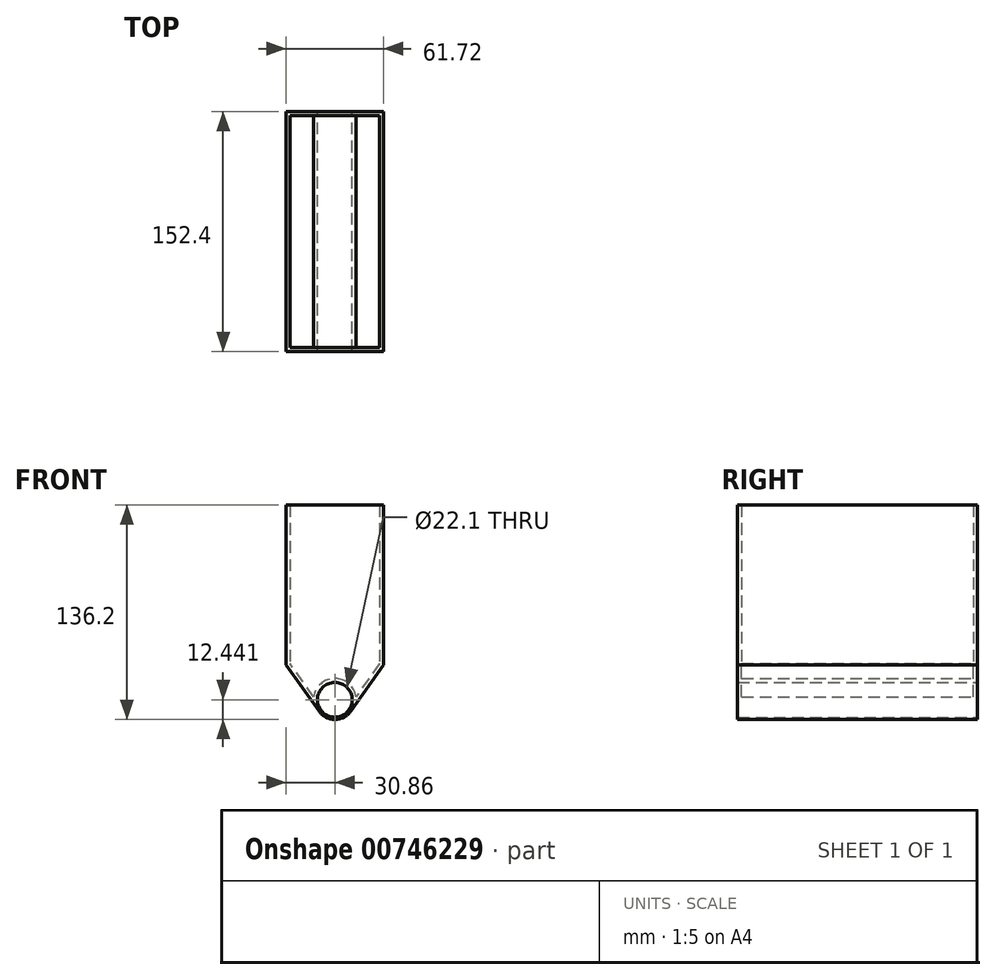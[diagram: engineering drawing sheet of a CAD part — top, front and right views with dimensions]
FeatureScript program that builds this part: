
annotation { "Feature Type Name" : "Feature", "Feature Type Description" : "" }
export const myFeature = defineFeature(function(context is Context, id is Id, definition is map)
    precondition{}
    {
        {
            var Q0;
            Q0=qCreatedBy(makeId("Front.planeOp"),FACE);
            var sketch = newSketch(context, id + "F0", { "sketchPlane" : qUnion([Q0])});
            skCircle(sketch, "E0", {"center": v(0, -33.74) * mm, "radius": 12.45 * mm});
            skCircle(sketch, "E1", {"center": v(0, -33.74) * mm, "radius": 11.05 * mm});
            skLineSegment(sketch, "E2", {"start": v(-10.17, -40.91) * mm, "end": v(-30.86, -11.58) * mm});
            skLineSegment(sketch, "E3", {"start": v(-30.86, -11.58) * mm, "end": v(0, -11.58) * mm});
            skLineSegment(sketch, "E4", {"start": v(30.86, -11.58) * mm, "end": v(0, -11.58) * mm});
            skLineSegment(sketch, "E5", {"start": v(30.86, -11.58) * mm, "end": v(10.17, -40.91) * mm});
            skSolve(sketch);
        }
        {
            var Q0;
            Q0 = qSketchRegion(id + "F0", true);
            extrude(context, id + "F1", {"entities" : qUnion([Q0]), "depth" : 76.2 * mm, "offsetDistance" : 25.4 * mm, "hasSecondDirection" : true, "secondDirectionOppositeDirection" : true, "secondDirectionDepth" : 76.2 * mm});
        }
        {
            var Q0;
            Q0=makeQuery(id+"F1.opExtrude","SWEPT_FACE",FACE,{"disambiguationData":[OSD([sQuery(id+"F0.wireOp",EDGE,"E3"),sQuery(id+"F0.wireOp",EDGE,"E4")])]});
            var sketch = newSketch(context, id + "F2", { "sketchPlane" : qUnion([Q0])});
            skLineSegment(sketch, "E6.bottom", {"start": v(30.86, 76.2) * mm, "end": v(-30.86, 76.2) * mm});
            skLineSegment(sketch, "E6.top", {"start": v(30.86, -76.2) * mm, "end": v(-30.86, -76.2) * mm});
            skLineSegment(sketch, "E6.left", {"start": v(30.86, 76.2) * mm, "end": v(30.86, -76.2) * mm});
            skLineSegment(sketch, "E6.right", {"start": v(-30.86, 76.2) * mm, "end": v(-30.86, -76.2) * mm});
            skSolve(sketch);
        }
        {
            var Q0;
            Q0 = qSketchRegion(id + "F2", true);
            extrude(context, id + "F3", {"entities" : qUnion([Q0]), "operationType" : NewBodyOperationType.ADD, "depth" : 101.6 * mm, "offsetDistance" : 25.4 * mm});
        }
        {
            var Q0;
            Q0=makeQuery(id+"F3.opExtrude","CAP_FACE",FACE,{"disambiguationData":[OSD([sQuery(id+"F2.wireOp",EDGE,"E6.bottom"),sQuery(id+"F2.wireOp",EDGE,"E6.top"),sQuery(id+"F2.wireOp",EDGE,"E6.left"),sQuery(id+"F2.wireOp",EDGE,"E6.right")])],"isStart":false});
            shell(context, id + "F4", {"entities" : qUnion([Q0]), "thickness" : 2.54 * mm});
        }
    });
